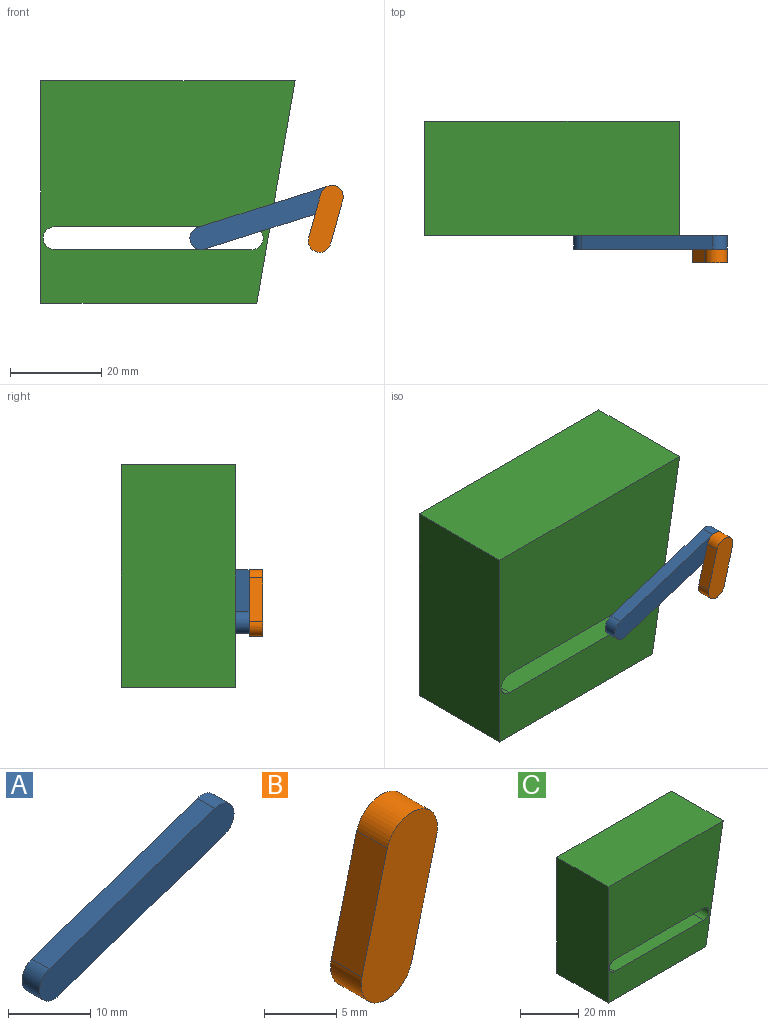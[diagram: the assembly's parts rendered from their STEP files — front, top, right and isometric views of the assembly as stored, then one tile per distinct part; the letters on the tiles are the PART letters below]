
ASSEMBLY  parts=3 mates=2
PART A: 6 faces, bbox 33.4x3x14.7 mm
  f0: plane 28.39x9.68mm, normal (0.32,0,-0.95), area 90mm2, adj f1,f3,f4,f5
  f1: cylinder r=2.5mm len=4.87mm, axis (0,-1,0), area 23.6mm2, adj f0,f2,f4,f5
  f2: plane 28.39x9.68mm, normal (-0.32,0,0.95), area 90mm2, adj f1,f3,f4,f5
  f3: cylinder r=2.5mm len=4.87mm, axis (0,-1,0), area 23.6mm2, adj f0,f2,f4,f5
  f4: plane 33.39x14.68mm, normal (0,1,0), area 169.6mm2, adj f0,f1,f2,f3
  f5: plane 33.39x14.68mm, normal (0,-1,0), area 169.6mm2, adj f0,f1,f2,f3
PART B: 6 faces, bbox 7.5x3x14.7 mm
  f0: plane 9.68x3mm, normal (0.97,0,-0.25), area 30mm2, adj f1,f3,f4,f5
  f1: cylinder r=2.5mm len=4.92mm, axis (0,1,0), area 23.6mm2, adj f0,f2,f4,f5
  f2: plane 9.68x3mm, normal (-0.97,0,0.25), area 30mm2, adj f1,f3,f4,f5
  f3: cylinder r=2.5mm len=4.92mm, axis (0,1,0), area 23.6mm2, adj f0,f2,f4,f5
  f4: plane 14.68x7.5mm, normal (0,-1,0), area 69.6mm2, adj f0,f1,f2,f3
  f5: plane 14.68x7.5mm, normal (0,1,0), area 69.6mm2, adj f0,f1,f2,f3
PART C: 10 faces, bbox 55.7x25x48.7 mm
  f0: plane 55.74x48.75mm, normal (0,1,0), area 2276mm2, adj f2,f3,f4,f5,f6,f7,f8,f9
  f1: plane 55.74x48.75mm, normal (0,-1,0), area 2276mm2, adj f2,f3,f4,f5,f6,f7,f8,f9
  f2: plane 55.74x25mm, normal (0,0,1), area 1393.4mm2, adj f0,f1,f3,f5
  f3: plane 48.75x25mm, normal (0.99,0,-0.17), area 1236.6mm2, adj f0,f1,f2,f4
  f4: plane 47.32x25mm, normal (0,0,-1), area 1183.1mm2, adj f0,f1,f3,f5
  f5: plane 48.75x25mm, normal (-1,0,0), area 1218.6mm2, adj f0,f1,f2,f4
  f6: plane 43.24x25mm, normal (0,0,-1), area 1080.9mm2, adj f0,f1,f7,f8
  f7: cylinder r=2.5mm len=25mm, axis (0,-1,0), area 196.3mm2, adj f0,f1,f6,f9
  f8: cylinder r=2.5mm len=25mm, axis (0,-1,0), area 196.3mm2, adj f0,f1,f6,f9
  f9: plane 43.24x25mm, normal (0,0,1), area 1080.9mm2, adj f0,f1,f7,f8
PLACE A rot(axis=(0,1,0),1.3deg) t=(-0.05,3,0.01)mm
PLACE B rot(axis=(0,1,0),1deg) t=(0,3,0)mm
PLACE C t=(12.44,3,0.58)mm fixed
MATE pin_slot A.f3 <-> C.f8  axis (0,1,0) through (-25.94,6,0.58)mm
MATE revolute B.f1 <-> A.f1  axis (0,1,0) through (2.66,3,9.64)mm
